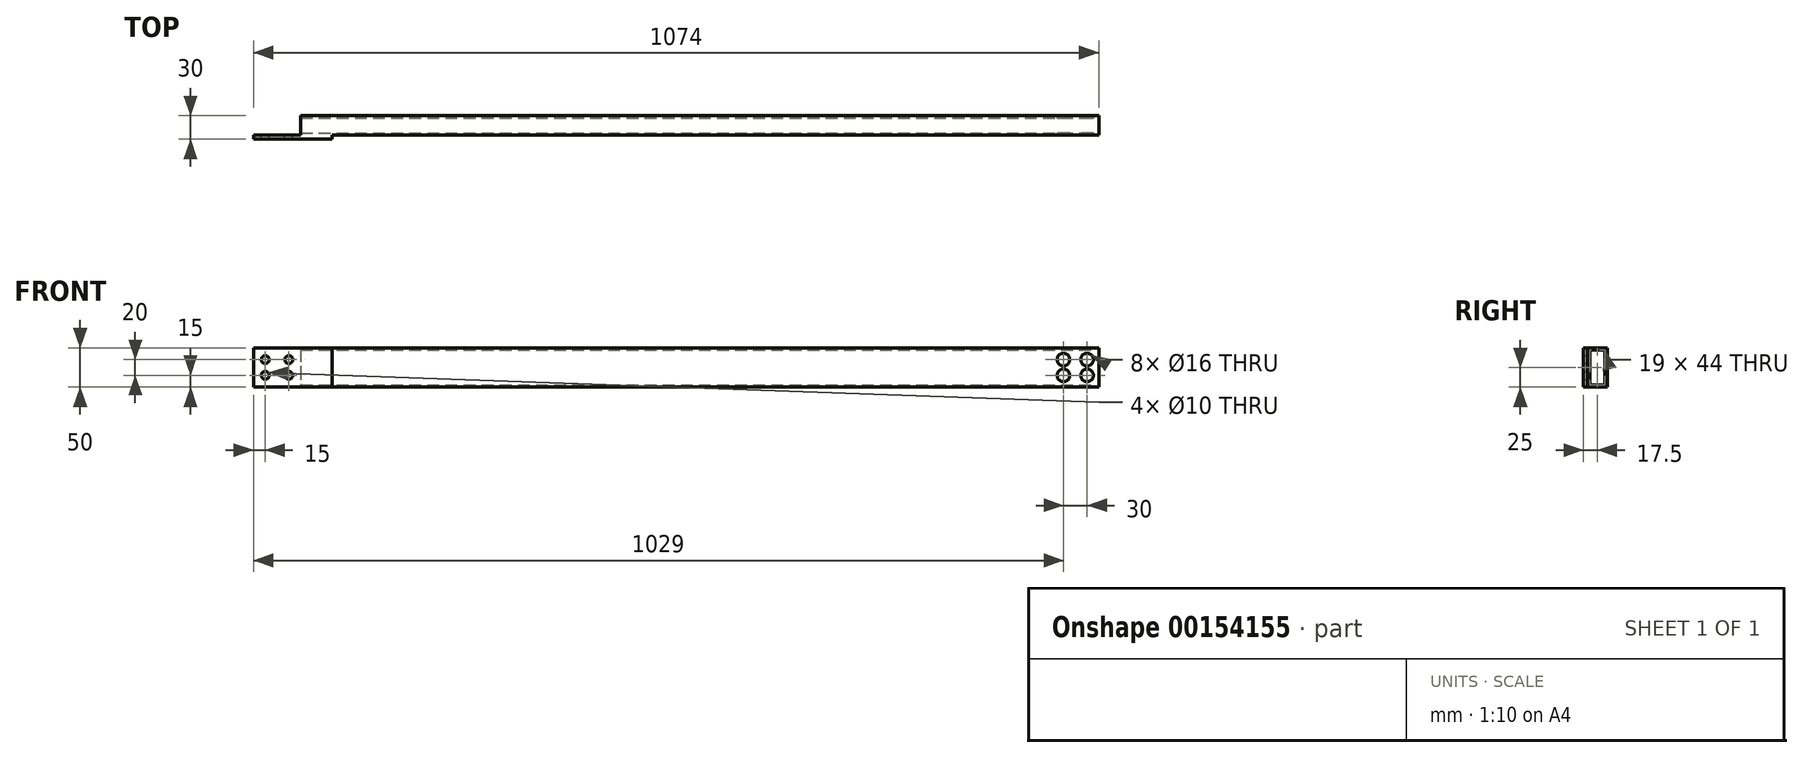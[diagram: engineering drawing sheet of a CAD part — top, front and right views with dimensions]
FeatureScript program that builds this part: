
annotation { "Feature Type Name" : "Feature", "Feature Type Description" : "" }
export const myFeature = defineFeature(function(context is Context, id is Id, definition is map)
    precondition{}
    {
        {
            var Q0;
            Q0=qCreatedBy(makeId("Front.planeOp"),FACE);
            var sketch = newSketch(context, id + "F0", { "sketchPlane" : qUnion([Q0])});
            skLineSegment(sketch, "E0.bottom", {"start": v(507, 25) * mm, "end": v(-507, 25) * mm});
            skLineSegment(sketch, "E0.top", {"start": v(507, -25) * mm, "end": v(-507, -25) * mm});
            skLineSegment(sketch, "E0.left", {"start": v(507, 25) * mm, "end": v(507, -25) * mm});
            skLineSegment(sketch, "E0.right", {"start": v(-507, 25) * mm, "end": v(-507, -25) * mm});
            skPoint(sketch, "E0.middle", {"position": v(0, 0) * mm});
            skSolve(sketch);
        }
        {
            var Q0;
            Q0 = qSketchRegion(id + "F0", true);
            extrude(context, id + "F1", {"entities" : qUnion([Q0]), "depth" : 25 * mm});
        }
        {
            var Q0;
            Q0=makeQuery(id+"F1.opExtrude","CAP_FACE",FACE,{"disambiguationData":[OSD([sQuery(id+"F0.wireOp",EDGE,"E0.bottom"),sQuery(id+"F0.wireOp",EDGE,"E0.top"),sQuery(id+"F0.wireOp",EDGE,"E0.left"),sQuery(id+"F0.wireOp",EDGE,"E0.right")])],"isStart":false});
            var sketch = newSketch(context, id + "F2", { "sketchPlane" : qUnion([Q0])});
            skPoint(sketch, "E1", {"position": v(492, 10) * mm});
            skPoint(sketch, "E2", {"position": v(492, -10) * mm});
            skPoint(sketch, "E3", {"position": v(462, -10) * mm});
            skPoint(sketch, "E4", {"position": v(462, 10) * mm});
            skCircle(sketch, "E5", {"center": v(462, 10) * mm, "radius": 8 * mm});
            skCircle(sketch, "E6", {"center": v(462, -10) * mm, "radius": 8 * mm});
            skCircle(sketch, "E7", {"center": v(492, 10) * mm, "radius": 8 * mm});
            skCircle(sketch, "E8", {"center": v(492, -10) * mm, "radius": 8 * mm});
            skSolve(sketch);
        }
        {
            var Q0;
            Q0 = qSketchRegion(id + "F2", true);
            extrude(context, id + "F3", {"entities" : qUnion([Q0]), "operationType" : NewBodyOperationType.REMOVE, "oppositeDirection" : true, "depth" : 25 * mm});
        }
        {
            var Q0;
            Q0=makeQuery(id+"F1.opExtrude","SWEPT_FACE",FACE,{"disambiguationData":[OSD([sQuery(id+"F0.wireOp",EDGE,"E0.left")])]});
            var sketch = newSketch(context, id + "F4", { "sketchPlane" : qUnion([Q0])});
            skLineSegment(sketch, "E9.0", {"start": v(-25, 25) * mm, "end": v(0, 25) * mm});
            skLineSegment(sketch, "E10.0", {"start": v(-25, 25) * mm, "end": v(-25, -25) * mm});
            skLineSegment(sketch, "E11.0", {"start": v(-25, -25) * mm, "end": v(0, -25) * mm});
            skLineSegment(sketch, "E12.0", {"start": v(0, 25) * mm, "end": v(0, -25) * mm});
            skLineSegment(sketch, "E13.0", {"start": v(-22, 22) * mm, "end": v(-3, 22) * mm});
            skLineSegment(sketch, "E13.1", {"start": v(-22, 22) * mm, "end": v(-22, -22) * mm});
            skLineSegment(sketch, "E13.2", {"start": v(-22, -22) * mm, "end": v(-3, -22) * mm});
            skLineSegment(sketch, "E13.3", {"start": v(-3, 22) * mm, "end": v(-3, -22) * mm});
            skSolve(sketch);
        }
        {
            var Q0;
            Q0=makeQuery(id+"F4.imprint","IMPRINT",FACE,{"disambiguationData":[TD([[makeQuery(id+"F4.imprint","IMPRINT",EDGE,{"derivedFrom":sQuery(id+"F4.wireOp",EDGE,"E13.0")}),-1.0]])]});
            extrude(context, id + "F5", {"entities" : qUnion([Q0]), "operationType" : NewBodyOperationType.REMOVE, "oppositeDirection" : true, "depth" : 1014 * mm});
        }
        {
            var Q0;
            Q0=makeQuery(id+"F1.opExtrude","CAP_FACE",FACE,{"disambiguationData":[OSD([sQuery(id+"F0.wireOp",EDGE,"E0.bottom"),sQuery(id+"F0.wireOp",EDGE,"E0.top"),sQuery(id+"F0.wireOp",EDGE,"E0.left"),sQuery(id+"F0.wireOp",EDGE,"E0.right")])],"isStart":false});
            var sketch = newSketch(context, id + "F6", { "sketchPlane" : qUnion([Q0])});
            skPoint(sketch, "E14", {"position": v(-467, 25) * mm});
            skLineSegment(sketch, "E15.bottom", {"start": v(-467, 25) * mm, "end": v(-567, 25) * mm});
            skLineSegment(sketch, "E15.top", {"start": v(-467, -25) * mm, "end": v(-567, -25) * mm});
            skLineSegment(sketch, "E15.left", {"start": v(-467, 25) * mm, "end": v(-467, -25) * mm});
            skLineSegment(sketch, "E15.right", {"start": v(-567, 25) * mm, "end": v(-567, -25) * mm});
            skPoint(sketch, "E16", {"position": v(-552, 10) * mm});
            skPoint(sketch, "E17", {"position": v(-552, -10) * mm});
            skPoint(sketch, "E18", {"position": v(-522, 10) * mm});
            skPoint(sketch, "E19", {"position": v(-522, -10) * mm});
            skCircle(sketch, "E20", {"center": v(-552, 10) * mm, "radius": 5 * mm});
            skCircle(sketch, "E21", {"center": v(-552, -10) * mm, "radius": 5 * mm});
            skCircle(sketch, "E22", {"center": v(-522, -10) * mm, "radius": 5 * mm});
            skCircle(sketch, "E23", {"center": v(-522, 10) * mm, "radius": 5 * mm});
            skSolve(sketch);
        }
        {
            var Q0;
            Q0 = qSketchRegion(id + "F6", true);
            extrude(context, id + "F7", {"entities" : qUnion([Q0]), "operationType" : NewBodyOperationType.ADD, "depth" : 5 * mm});
        }
    });
